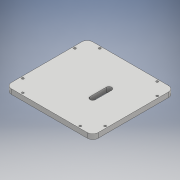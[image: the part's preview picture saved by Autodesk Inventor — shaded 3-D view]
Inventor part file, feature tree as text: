
AUTODESK INVENTOR PART (.ipt)
format: ipt  version: 2017 (Build 210142000, 142)  size: 290,816 bytes
history: native  units: mm
features: extrude x2, sketch x2, other x1
ambient origin geometry x8: Origin, YZ Plane, XZ Plane, XY Plane, X Axis, Y Axis, Z Axis, Center Point
bodies: Body1 (feature_tree)
feature tree (5):
  extrude  "Estrusione2"  Depth=10.0mm
  sketch  "Schizzo2"
  other  "Sposta corpo1"
  extrude  "Estrusione3"  Depth=4.0mm
  sketch  "Schizzo1"
